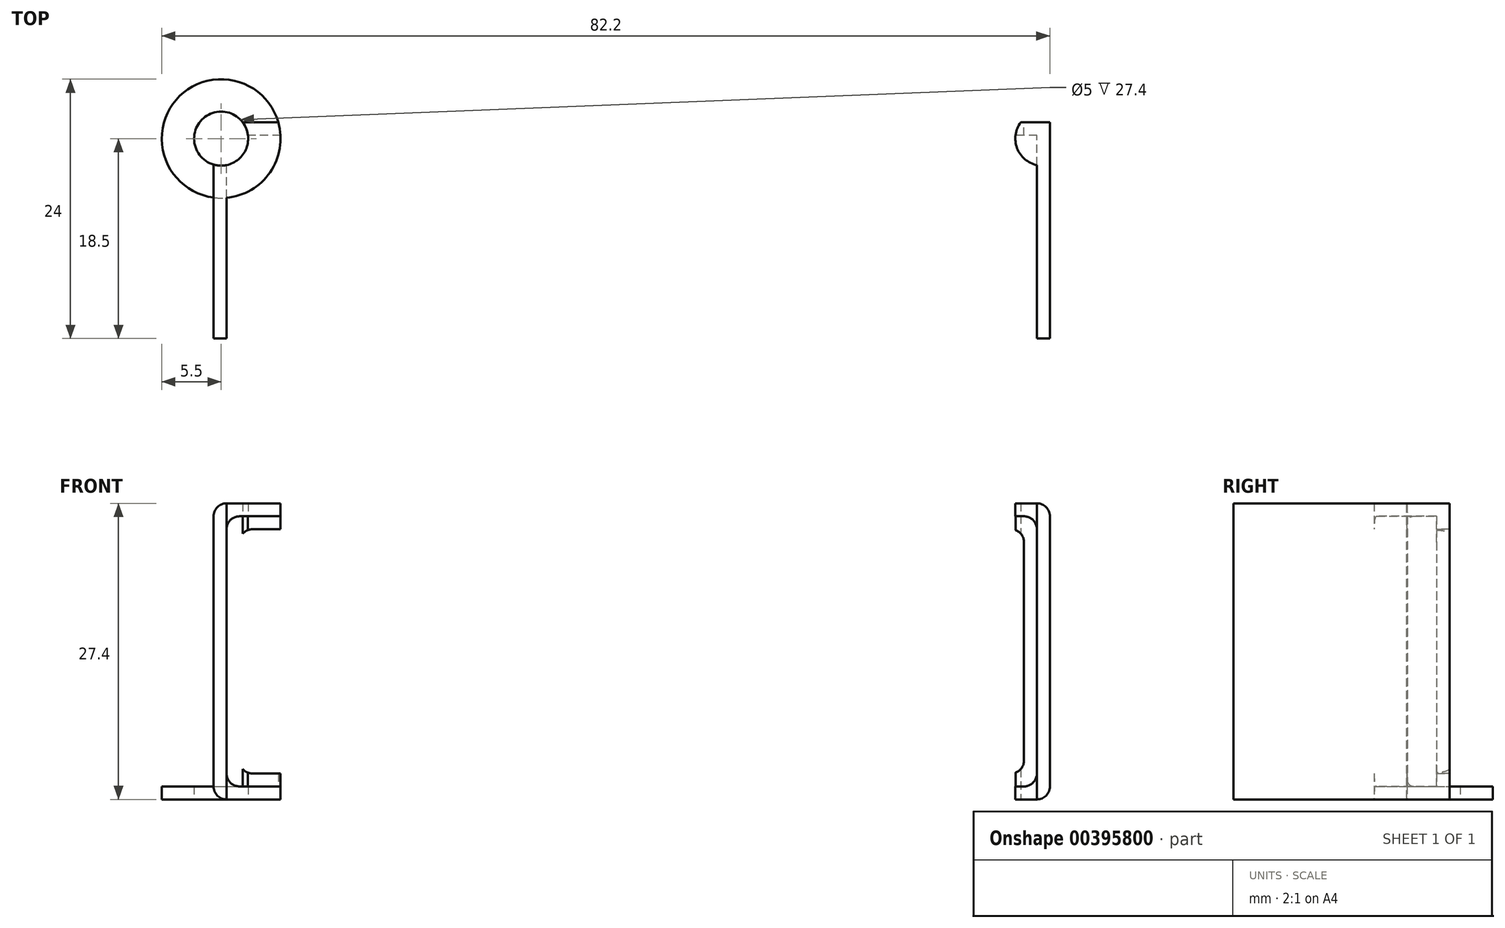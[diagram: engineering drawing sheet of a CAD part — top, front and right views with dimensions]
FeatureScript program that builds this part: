
annotation { "Feature Type Name" : "Feature", "Feature Type Description" : "" }
export const myFeature = defineFeature(function(context is Context, id is Id, definition is map)
    precondition{}
    {
        {
            var Q0;
            Q0=qCreatedBy(makeId("Front.planeOp"),FACE);
            var sketch = newSketch(context, id + "F0", { "sketchPlane" : qUnion([Q0])});
            skLineSegment(sketch, "E0.bottom", {"start": v(36.3, 12.5) * mm, "end": v(-36.3, 12.5) * mm});
            skLineSegment(sketch, "E0.top", {"start": v(36.3, -12.5) * mm, "end": v(-36.3, -12.5) * mm});
            skLineSegment(sketch, "E0.left", {"start": v(37.5, 11.3) * mm, "end": v(37.5, -11.3) * mm});
            skLineSegment(sketch, "E0.right", {"start": v(-37.5, 11.3) * mm, "end": v(-37.5, -11.3) * mm});
            skPoint(sketch, "E0.middle", {"position": v(0, 0) * mm});
            skLineSegment(sketch, "E1.bottom", {"start": v(37.5, 13.7) * mm, "end": v(-37.5, 13.7) * mm});
            skLineSegment(sketch, "E1.top", {"start": v(37.5, -13.7) * mm, "end": v(-37.5, -13.7) * mm});
            skLineSegment(sketch, "E1.left", {"start": v(38.7, 12.5) * mm, "end": v(38.7, -12.5) * mm});
            skLineSegment(sketch, "E1.right", {"start": v(-38.7, 12.5) * mm, "end": v(-38.7, -12.5) * mm});
            skLineSegment(sketch, "E2.0", {"start": v(35.1, 11.3) * mm, "end": v(-35.1, 11.3) * mm});
            skLineSegment(sketch, "E2.1", {"start": v(36.3, 10.1) * mm, "end": v(36.3, -10.1) * mm});
            skLineSegment(sketch, "E2.2", {"start": v(35.1, -11.3) * mm, "end": v(-35.1, -11.3) * mm});
            skLineSegment(sketch, "E2.3", {"start": v(-36.3, 10.1) * mm, "end": v(-36.3, -10.1) * mm});
            skPoint(sketch, "E3.visualSharp", {"position": v(-36.3, 11.3) * mm});
            skArc(sketch, "E3.filletArc", {"start": v(-35.1, 11.3) * mm, "mid": v(-35.95, 10.95) * mm, "end": v(-36.3, 10.1) * mm});
            skPoint(sketch, "E4.visualSharp", {"position": v(-37.5, 12.5) * mm});
            skArc(sketch, "E4.filletArc", {"start": v(-36.3, 12.5) * mm, "mid": v(-37.15, 12.15) * mm, "end": v(-37.5, 11.3) * mm});
            skPoint(sketch, "E5.visualSharp", {"position": v(-38.7, 13.7) * mm});
            skArc(sketch, "E5.filletArc", {"start": v(-37.5, 13.7) * mm, "mid": v(-38.35, 13.35) * mm, "end": v(-38.7, 12.5) * mm});
            skPoint(sketch, "E6.visualSharp", {"position": v(36.3, 11.3) * mm});
            skArc(sketch, "E6.filletArc", {"start": v(36.3, 10.1) * mm, "mid": v(35.95, 10.95) * mm, "end": v(35.1, 11.3) * mm});
            skPoint(sketch, "E7.visualSharp", {"position": v(37.5, 12.5) * mm});
            skArc(sketch, "E7.filletArc", {"start": v(37.5, 11.3) * mm, "mid": v(37.15, 12.15) * mm, "end": v(36.3, 12.5) * mm});
            skPoint(sketch, "E8.visualSharp", {"position": v(38.7, 13.7) * mm});
            skArc(sketch, "E8.filletArc", {"start": v(38.7, 12.5) * mm, "mid": v(38.35, 13.35) * mm, "end": v(37.5, 13.7) * mm});
            skPoint(sketch, "E9.visualSharp", {"position": v(38.7, -13.7) * mm});
            skArc(sketch, "E9.filletArc", {"start": v(37.5, -13.7) * mm, "mid": v(38.35, -13.35) * mm, "end": v(38.7, -12.5) * mm});
            skPoint(sketch, "E10.visualSharp", {"position": v(36.3, -11.3) * mm});
            skArc(sketch, "E10.filletArc", {"start": v(35.1, -11.3) * mm, "mid": v(35.95, -10.95) * mm, "end": v(36.3, -10.1) * mm});
            skArc(sketch, "E11.filletArc", {"start": v(36.3, -12.5) * mm, "mid": v(37.15, -12.15) * mm, "end": v(37.5, -11.3) * mm});
            skPoint(sketch, "E12.visualSharp", {"position": v(-38.7, -13.7) * mm});
            skArc(sketch, "E12.filletArc", {"start": v(-38.7, -12.5) * mm, "mid": v(-38.35, -13.35) * mm, "end": v(-37.5, -13.7) * mm});
            skPoint(sketch, "E13.visualSharp", {"position": v(-36.3, -11.3) * mm});
            skArc(sketch, "E13.filletArc", {"start": v(-36.3, -10.1) * mm, "mid": v(-35.95, -10.95) * mm, "end": v(-35.1, -11.3) * mm});
            skArc(sketch, "E14.filletArc", {"start": v(-37.5, -11.3) * mm, "mid": v(-37.15, -12.15) * mm, "end": v(-36.3, -12.5) * mm});
            skSolve(sketch);
        }
        {
            var Q0;
            Q0=makeQuery(id+"F0.imprint","IMPRINT",FACE,{"disambiguationData":[TD([[makeQuery(id+"F0.imprint","IMPRINT",EDGE,{"derivedFrom":sQuery(id+"F0.wireOp",EDGE,"E0.bottom")}),-1.0]])]});
            extrude(context, id + "F1", {"entities" : qUnion([Q0]), "depth" : 20 * mm});
        }
        {
            var Q0;
            Q0=makeQuery(id+"F0.imprint","IMPRINT",FACE,{"disambiguationData":[TD([[makeQuery(id+"F0.imprint","IMPRINT",EDGE,{"derivedFrom":sQuery(id+"F0.wireOp",EDGE,"E0.bottom")}),1.0]])]});
            extrude(context, id + "F2", {"entities" : qUnion([Q0]), "operationType" : NewBodyOperationType.ADD, "depth" : 1.2 * mm});
        }
        {
            var Q0;
            Q0=makeQuery(id+"F1.opExtrude","SWEPT_FACE",FACE,{"disambiguationData":[OSD([sQuery(id+"F0.wireOp",EDGE,"E1.top")])]});
            var sketch = newSketch(context, id + "F3", { "sketchPlane" : qUnion([Q0])});
            skCircle(sketch, "E15", {"center": v(-38, 1.5) * mm, "radius": 2.5 * mm});
            skCircle(sketch, "E16.MirrorC", {"center": v(38, 1.5) * mm, "radius": 2.5 * mm});
            skCircle(sketch, "E17.0", {"center": v(-38, 1.5) * mm, "radius": 5.5 * mm});
            skSolve(sketch);
        }
        {
            var Q0;
            Q0=makeQuery(id+"F3.imprint","IMPRINT",FACE,{"disambiguationData":[TD([[makeQuery(id+"F3.imprint","IMPRINT",EDGE,{"derivedFrom":sQuery(id+"F3.wireOp",EDGE,"E15")}),1.0]])]});
            var Q1;
            Q1=makeQuery(id+"F3.imprint","IMPRINT",FACE,{"disambiguationData":[TD([[makeQuery(id+"F3.imprint","IMPRINT",EDGE,{"derivedFrom":sQuery(id+"F3.wireOp",EDGE,"E16.MirrorC")}),-1.0]])]});
            extrude(context, id + "F4", {"entities" : qUnion([Q0, Q1]), "operationType" : NewBodyOperationType.REMOVE, "oppositeDirection" : true, "depth" : 30 * mm});
        }
        {
            var Q0;
            {var subQ1=sQuery(id+"F0.wireOp",EDGE,"E1.top");var subQ4=makeQuery(id+"F1.opExtrude","CAP_EDGE",EDGE,{"disambiguationData":[OSD([subQ1])],"isStart":true});var subQ6=sQuery(id+"F3.wireOp",EDGE,"E17.0");var subQ7=makeQuery(id+"F3.imprint","INTERSECT",VERTEX,{"derivedFrom":[subQ4,subQ6]});Q0=makeQuery(id+"F3.imprint","IMPRINT",FACE,{"disambiguationData":[TD([[makeQuery(id+"F3.imprint","IMPRINT",EDGE,{"disambiguationData":[TD([[subQ7,-1.0]])],"derivedFrom":subQ4}),1.0]])]});}
            extrude(context, id + "F5", {"entities" : qUnion([Q0]), "operationType" : NewBodyOperationType.ADD, "oppositeDirection" : true, "depth" : 1.2 * mm});
        }
    });
